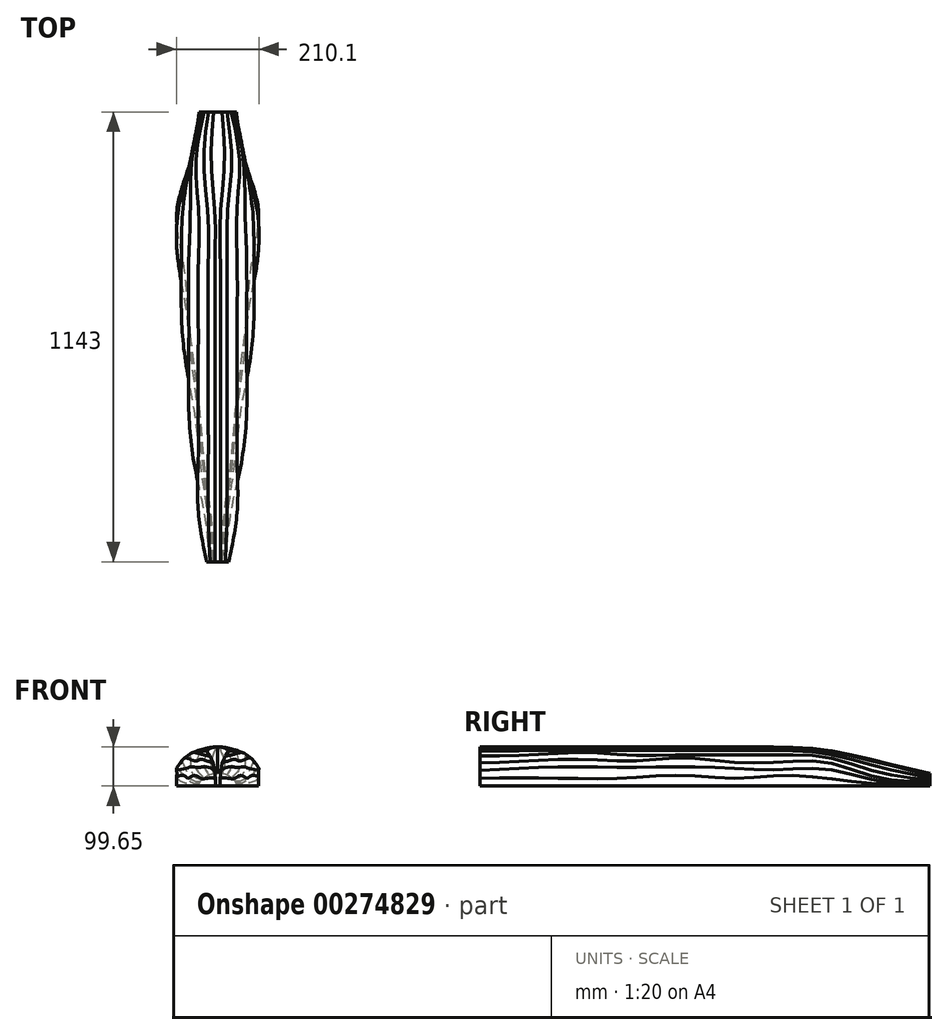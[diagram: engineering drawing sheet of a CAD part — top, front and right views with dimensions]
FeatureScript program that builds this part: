
annotation { "Feature Type Name" : "Feature", "Feature Type Description" : "" }
export const myFeature = defineFeature(function(context is Context, id is Id, definition is map)
    precondition{}
    {
        {
            var Q0;
            Q0=qCreatedBy(makeId("Front.planeOp"),FACE);
            cPlane(context, id + "F0", {"entities" : qUnion([Q0]), "cplaneType" : CPlaneType.OFFSET, "offset" : 127 * mm, "oppositeDirection" : true, "width" : 152.4 * mm, "height" : 152.4 * mm});
        }
        {
            var Q0;
            Q0=qCreatedBy(makeId("Front.planeOp"),FACE);
            cPlane(context, id + "F1", {"entities" : qUnion([Q0]), "cplaneType" : CPlaneType.OFFSET, "offset" : 254 * mm, "oppositeDirection" : true, "width" : 152.4 * mm, "height" : 152.4 * mm});
        }
        {
            var Q0;
            Q0=qCreatedBy(makeId("Front.planeOp"),FACE);
            cPlane(context, id + "F2", {"entities" : qUnion([Q0]), "cplaneType" : CPlaneType.OFFSET, "offset" : 381 * mm, "oppositeDirection" : true, "width" : 152.4 * mm, "height" : 152.4 * mm});
        }
        {
            var Q0;
            Q0=qCreatedBy(makeId("Front.planeOp"),FACE);
            cPlane(context, id + "F3", {"entities" : qUnion([Q0]), "cplaneType" : CPlaneType.OFFSET, "offset" : 127 * mm, "width" : 152.4 * mm, "height" : 152.4 * mm});
        }
        {
            var Q0;
            Q0=qCreatedBy(makeId("Front.planeOp"),FACE);
            cPlane(context, id + "F4", {"entities" : qUnion([Q0]), "cplaneType" : CPlaneType.OFFSET, "offset" : 254 * mm, "width" : 152.4 * mm, "height" : 152.4 * mm});
        }
        {
            var Q0;
            Q0=qCreatedBy(makeId("Front.planeOp"),FACE);
            cPlane(context, id + "F5", {"entities" : qUnion([Q0]), "cplaneType" : CPlaneType.OFFSET, "offset" : 381 * mm, "width" : 152.4 * mm, "height" : 152.4 * mm});
        }
        {
            var Q0;
            Q0=qCreatedBy(makeId("Front.planeOp"),FACE);
            cPlane(context, id + "F6", {"entities" : qUnion([Q0]), "cplaneType" : CPlaneType.OFFSET, "offset" : 508 * mm, "width" : 152.4 * mm, "height" : 152.4 * mm});
        }
        {
            var Q0;
            Q0=qCreatedBy(id+"F2.planeOp",FACE);
            var sketch = newSketch(context, id + "F7", { "sketchPlane" : qUnion([Q0])});
            skLineSegment(sketch, "E0", {"start": v(-55.45, -58.67) * mm, "end": v(48.5, -58.67) * mm});
            skLineSegment(sketch, "E1", {"start": v(48.5, -58.67) * mm, "end": v(48.5, -39.44) * mm});
            skLineSegment(sketch, "E2", {"start": v(48.5, -39.44) * mm, "end": v(45.16, -16.7) * mm});
            skLineSegment(sketch, "E3", {"start": v(45.16, -16.7) * mm, "end": v(33.42, 0) * mm});
            skLineSegment(sketch, "E4", {"start": v(33.42, 0) * mm, "end": v(13.96, 12.38) * mm});
            skLineSegment(sketch, "E5", {"start": v(13.96, 12.38) * mm, "end": v(-7.08, 22.02) * mm});
            skLineSegment(sketch, "E6", {"start": v(-7.08, 22.02) * mm, "end": v(-30.27, 29.1) * mm});
            skLineSegment(sketch, "E7", {"start": v(-30.27, 29.1) * mm, "end": v(-48.16, 31.65) * mm});
            skLineSegment(sketch, "E8", {"start": v(-48.16, 31.65) * mm, "end": v(-55.45, 31.65) * mm});
            skLineSegment(sketch, "E9", {"start": v(-55.45, 31.65) * mm, "end": v(-55.45, -58.67) * mm});
            skSolve(sketch);
        }
        {
            var Q0;
            Q0=qCreatedBy(id+"F1.planeOp",FACE);
            var sketch = newSketch(context, id + "F8", { "sketchPlane" : qUnion([Q0])});
            skLineSegment(sketch, "E10", {"start": v(-55.45, -58.67) * mm, "end": v(31.61, -58.67) * mm});
            skLineSegment(sketch, "E11", {"start": v(31.61, -58.67) * mm, "end": v(31.61, -32) * mm});
            skLineSegment(sketch, "E12", {"start": v(31.61, -32) * mm, "end": v(44.98, -17.07) * mm});
            skLineSegment(sketch, "E13", {"start": v(44.98, -17.07) * mm, "end": v(36.88, 2.51) * mm});
            skLineSegment(sketch, "E14", {"start": v(36.88, 2.51) * mm, "end": v(18.07, 20.36) * mm});
            skLineSegment(sketch, "E15", {"start": v(18.07, 20.36) * mm, "end": v(-6.04, 31.25) * mm});
            skLineSegment(sketch, "E16", {"start": v(-6.04, 31.25) * mm, "end": v(-31.47, 38.05) * mm});
            skLineSegment(sketch, "E17", {"start": v(-31.47, 38.05) * mm, "end": v(-48.7, 40.66) * mm});
            skLineSegment(sketch, "E18", {"start": v(-48.7, 40.66) * mm, "end": v(-55.45, 40.66) * mm});
            skLineSegment(sketch, "E19", {"start": v(-55.45, 40.66) * mm, "end": v(-55.45, -58.67) * mm});
            skSolve(sketch);
        }
        {
            var Q0;
            Q0=qCreatedBy(id+"F0.planeOp",FACE);
            var sketch = newSketch(context, id + "F9", { "sketchPlane" : qUnion([Q0])});
            skLineSegment(sketch, "E20", {"start": v(-55.45, -58.67) * mm, "end": v(19.66, -58.67) * mm});
            skLineSegment(sketch, "E21", {"start": v(19.66, -58.67) * mm, "end": v(19.66, -38.92) * mm});
            skLineSegment(sketch, "E22", {"start": v(19.66, -38.92) * mm, "end": v(22.96, -13.33) * mm});
            skLineSegment(sketch, "E23", {"start": v(22.96, -13.33) * mm, "end": v(36.88, 2.51) * mm});
            skLineSegment(sketch, "E24", {"start": v(36.88, 2.51) * mm, "end": v(18.07, 20.36) * mm});
            skLineSegment(sketch, "E25", {"start": v(18.07, 20.36) * mm, "end": v(-6.04, 31.25) * mm});
            skLineSegment(sketch, "E26", {"start": v(-6.04, 31.25) * mm, "end": v(-31.47, 38.05) * mm});
            skLineSegment(sketch, "E27", {"start": v(-31.47, 38.05) * mm, "end": v(-48.7, 40.66) * mm});
            skLineSegment(sketch, "E28", {"start": v(-48.7, 40.66) * mm, "end": v(-55.45, 40.66) * mm});
            skLineSegment(sketch, "E29", {"start": v(-55.45, 40.66) * mm, "end": v(-55.45, -58.67) * mm});
            skSolve(sketch);
        }
        {
            var Q0;
            Q0=qCreatedBy(makeId("Front.planeOp"),FACE);
            var sketch = newSketch(context, id + "F10", { "sketchPlane" : qUnion([Q0])});
            skLineSegment(sketch, "E30", {"start": v(-55.45, -58.67) * mm, "end": v(4.91, -58.67) * mm});
            skLineSegment(sketch, "E31", {"start": v(4.91, -58.67) * mm, "end": v(4.91, -31.45) * mm});
            skLineSegment(sketch, "E32", {"start": v(4.91, -31.45) * mm, "end": v(10.42, -9.63) * mm});
            skLineSegment(sketch, "E33", {"start": v(10.42, -9.63) * mm, "end": v(26.15, 12.58) * mm});
            skLineSegment(sketch, "E34", {"start": v(26.15, 12.58) * mm, "end": v(18.28, 20.25) * mm});
            skLineSegment(sketch, "E35", {"start": v(18.28, 20.25) * mm, "end": v(-6.04, 31.25) * mm});
            skLineSegment(sketch, "E36", {"start": v(-6.04, 31.25) * mm, "end": v(-31.47, 38.05) * mm});
            skLineSegment(sketch, "E37", {"start": v(-31.47, 38.05) * mm, "end": v(-48.7, 40.66) * mm});
            skLineSegment(sketch, "E38", {"start": v(-48.7, 40.66) * mm, "end": v(-55.45, 40.66) * mm});
            skLineSegment(sketch, "E39", {"start": v(-55.45, 40.66) * mm, "end": v(-55.45, -58.67) * mm});
            skSolve(sketch);
        }
        {
            var Q0;
            Q0=qCreatedBy(id+"F3.planeOp",FACE);
            var sketch = newSketch(context, id + "F11", { "sketchPlane" : qUnion([Q0])});
            skLineSegment(sketch, "E40", {"start": v(-55.45, -58.67) * mm, "end": v(-10.42, -58.67) * mm});
            skLineSegment(sketch, "E41", {"start": v(-10.42, -58.67) * mm, "end": v(-10.42, -38.14) * mm});
            skLineSegment(sketch, "E42", {"start": v(-10.42, -38.14) * mm, "end": v(-6.1, -11.8) * mm});
            skLineSegment(sketch, "E43", {"start": v(-6.1, -11.8) * mm, "end": v(3.34, 4.72) * mm});
            skLineSegment(sketch, "E44", {"start": v(3.34, 4.72) * mm, "end": v(18.09, 20.05) * mm});
            skLineSegment(sketch, "E45", {"start": v(18.09, 20.05) * mm, "end": v(-6.04, 31.25) * mm});
            skLineSegment(sketch, "E46", {"start": v(-6.04, 31.25) * mm, "end": v(-31.47, 38.05) * mm});
            skLineSegment(sketch, "E47", {"start": v(-31.47, 38.05) * mm, "end": v(-48.7, 40.66) * mm});
            skLineSegment(sketch, "E48", {"start": v(-48.7, 40.66) * mm, "end": v(-55.45, 40.66) * mm});
            skLineSegment(sketch, "E49", {"start": v(-55.45, 40.66) * mm, "end": v(-55.45, -58.67) * mm});
            skSolve(sketch);
        }
        {
            var Q0;
            Q0=qCreatedBy(id+"F4.planeOp",FACE);
            var sketch = newSketch(context, id + "F12", { "sketchPlane" : qUnion([Q0])});
            skLineSegment(sketch, "E50", {"start": v(-55.45, -58.67) * mm, "end": v(-21.43, -58.67) * mm});
            skLineSegment(sketch, "E51", {"start": v(-21.43, -58.67) * mm, "end": v(-21.43, -39.9) * mm});
            skLineSegment(sketch, "E52", {"start": v(-21.43, -39.9) * mm, "end": v(-17.5, -9.83) * mm});
            skLineSegment(sketch, "E53", {"start": v(-17.5, -9.83) * mm, "end": v(-11.2, 9.24) * mm});
            skLineSegment(sketch, "E54", {"start": v(-11.2, 9.24) * mm, "end": v(5.11, 26.34) * mm});
            skLineSegment(sketch, "E55", {"start": v(5.11, 26.34) * mm, "end": v(-6.04, 31.25) * mm});
            skLineSegment(sketch, "E56", {"start": v(-6.04, 31.25) * mm, "end": v(-31.47, 38.05) * mm});
            skLineSegment(sketch, "E57", {"start": v(-31.47, 38.05) * mm, "end": v(-48.7, 40.66) * mm});
            skLineSegment(sketch, "E58", {"start": v(-48.7, 40.66) * mm, "end": v(-55.45, 40.66) * mm});
            skLineSegment(sketch, "E59", {"start": v(-55.45, 40.66) * mm, "end": v(-55.45, -58.67) * mm});
            skSolve(sketch);
        }
        {
            var Q0;
            Q0=qCreatedBy(id+"F5.planeOp",FACE);
            var sketch = newSketch(context, id + "F13", { "sketchPlane" : qUnion([Q0])});
            skLineSegment(sketch, "E60", {"start": v(-55.45, -58.67) * mm, "end": v(-37.94, -58.67) * mm});
            skLineSegment(sketch, "E61", {"start": v(-37.94, -58.67) * mm, "end": v(-37.94, -37.94) * mm});
            skLineSegment(sketch, "E62", {"start": v(-37.94, -37.94) * mm, "end": v(-34.4, -12) * mm});
            skLineSegment(sketch, "E63", {"start": v(-34.4, -12) * mm, "end": v(-29.68, 4.91) * mm});
            skLineSegment(sketch, "E64", {"start": v(-21.23, 20.05) * mm, "end": v(-29.68, 4.91) * mm});
            skLineSegment(sketch, "E65", {"start": v(-21.23, 20.05) * mm, "end": v(-6.04, 31.25) * mm});
            skLineSegment(sketch, "E66", {"start": v(-6.04, 31.25) * mm, "end": v(-31.47, 38.05) * mm});
            skLineSegment(sketch, "E67", {"start": v(-31.47, 38.05) * mm, "end": v(-48.7, 40.66) * mm});
            skLineSegment(sketch, "E68", {"start": v(-48.7, 40.66) * mm, "end": v(-55.45, 40.66) * mm});
            skLineSegment(sketch, "E69", {"start": v(-55.45, 40.66) * mm, "end": v(-55.45, -58.67) * mm});
            skSolve(sketch);
        }
        {
            var Q0;
            Q0=qCreatedBy(id+"F6.planeOp",FACE);
            var sketch = newSketch(context, id + "F14", { "sketchPlane" : qUnion([Q0])});
            skLineSegment(sketch, "E70", {"start": v(-55.45, -58.67) * mm, "end": v(-49.54, -58.67) * mm});
            skLineSegment(sketch, "E71", {"start": v(-49.54, -58.67) * mm, "end": v(-49.54, -39.71) * mm});
            skLineSegment(sketch, "E72", {"start": v(-49.54, -39.71) * mm, "end": v(-47.18, -19.27) * mm});
            skLineSegment(sketch, "E73", {"start": v(-47.18, -19.27) * mm, "end": v(-43.84, 0) * mm});
            skLineSegment(sketch, "E74", {"start": v(-43.84, 0) * mm, "end": v(-35.98, 18.48) * mm});
            skLineSegment(sketch, "E75", {"start": v(-35.98, 18.48) * mm, "end": v(-27.52, 30.47) * mm});
            skLineSegment(sketch, "E76", {"start": v(-27.52, 30.47) * mm, "end": v(-35.78, 36.56) * mm});
            skLineSegment(sketch, "E77", {"start": v(-35.78, 36.56) * mm, "end": v(-48.7, 40.66) * mm});
            skLineSegment(sketch, "E78", {"start": v(-48.7, 40.66) * mm, "end": v(-55.45, 40.66) * mm});
            skLineSegment(sketch, "E79", {"start": v(-55.45, 40.66) * mm, "end": v(-55.45, -58.67) * mm});
            skSolve(sketch);
        }
        {
            var Q0;
            Q0=qCreatedBy(makeId("Front.planeOp"),FACE);
            cPlane(context, id + "F15", {"entities" : qUnion([Q0]), "cplaneType" : CPlaneType.OFFSET, "offset" : 508 * mm, "oppositeDirection" : true, "width" : 152.4 * mm, "height" : 152.4 * mm});
        }
        {
            var Q0;
            Q0=qCreatedBy(makeId("Front.planeOp"),FACE);
            cPlane(context, id + "F16", {"entities" : qUnion([Q0]), "cplaneType" : CPlaneType.OFFSET, "offset" : 635 * mm, "oppositeDirection" : true, "width" : 152.4 * mm, "height" : 152.4 * mm});
        }
        {
            var Q0;
            Q0=qCreatedBy(id+"F15.planeOp",FACE);
            var sketch = newSketch(context, id + "F17", { "sketchPlane" : qUnion([Q0])});
            skLineSegment(sketch, "E80", {"start": v(-55.45, -58.67) * mm, "end": v(14.39, -58.67) * mm});
            skLineSegment(sketch, "E81", {"start": v(14.39, -58.67) * mm, "end": v(14.39, -53.58) * mm});
            skLineSegment(sketch, "E82", {"start": v(14.39, -53.58) * mm, "end": v(14.63, -46.57) * mm});
            skLineSegment(sketch, "E83", {"start": v(14.63, -46.57) * mm, "end": v(14.59, -38.3) * mm});
            skLineSegment(sketch, "E84", {"start": v(14.59, -38.3) * mm, "end": v(10.13, -24.95) * mm});
            skLineSegment(sketch, "E85", {"start": v(10.13, -24.95) * mm, "end": v(0, -11.24) * mm});
            skLineSegment(sketch, "E86", {"start": v(0, -11.24) * mm, "end": v(-19.82, 0) * mm});
            skLineSegment(sketch, "E87", {"start": v(-19.82, 0) * mm, "end": v(-38.22, 2.96) * mm});
            skLineSegment(sketch, "E88", {"start": v(-38.22, 2.96) * mm, "end": v(-55.45, 2.96) * mm});
            skLineSegment(sketch, "E89", {"start": v(-55.45, 2.96) * mm, "end": v(-55.45, -58.67) * mm});
            skSolve(sketch);
        }
        {
            var Q0;
            Q0=qCreatedBy(id+"F16.planeOp",FACE);
            var sketch = newSketch(context, id + "F18", { "sketchPlane" : qUnion([Q0])});
            skLineSegment(sketch, "E90", {"start": v(-55.45, -58.67) * mm, "end": v(-8.16, -58.67) * mm});
            skLineSegment(sketch, "E91", {"start": v(-8.16, -58.67) * mm, "end": v(-8.16, -53.47) * mm});
            skLineSegment(sketch, "E92", {"start": v(-8.16, -53.47) * mm, "end": v(-8.94, -50.33) * mm});
            skLineSegment(sketch, "E93", {"start": v(-8.94, -50.33) * mm, "end": v(-10.52, -46.4) * mm});
            skLineSegment(sketch, "E94", {"start": v(-10.52, -46.4) * mm, "end": v(-14.25, -42.66) * mm});
            skLineSegment(sketch, "E95", {"start": v(-14.25, -42.66) * mm, "end": v(-20.94, -37.55) * mm});
            skLineSegment(sketch, "E96", {"start": v(-20.94, -37.55) * mm, "end": v(-32.14, -30.08) * mm});
            skLineSegment(sketch, "E97", {"start": v(-32.14, -30.08) * mm, "end": v(-44.72, -26.34) * mm});
            skLineSegment(sketch, "E98", {"start": v(-44.72, -26.34) * mm, "end": v(-55.45, -26.34) * mm});
            skLineSegment(sketch, "E99", {"start": v(-55.45, -26.34) * mm, "end": v(-55.45, -58.67) * mm});
            skSolve(sketch);
        }
        {
            var Q0;
            Q0=makeQuery(id+"F14.imprint","IMPRINT",FACE,{"disambiguationData":[TD([[makeQuery(id+"F14.imprint","IMPRINT",EDGE,{"derivedFrom":sQuery(id+"F14.wireOp",EDGE,"E70")}),1.0]])]});
            var Q1;
            Q1=makeQuery(id+"F13.imprint","IMPRINT",FACE,{"disambiguationData":[TD([[makeQuery(id+"F13.imprint","IMPRINT",EDGE,{"derivedFrom":sQuery(id+"F13.wireOp",EDGE,"E60")}),1.0]])]});
            var Q2;
            Q2=makeQuery(id+"F12.imprint","IMPRINT",FACE,{"disambiguationData":[TD([[makeQuery(id+"F12.imprint","IMPRINT",EDGE,{"derivedFrom":sQuery(id+"F12.wireOp",EDGE,"E50")}),1.0]])]});
            var Q3;
            Q3=makeQuery(id+"F11.imprint","IMPRINT",FACE,{"disambiguationData":[TD([[makeQuery(id+"F11.imprint","IMPRINT",EDGE,{"derivedFrom":sQuery(id+"F11.wireOp",EDGE,"E40")}),1.0]])]});
            var Q4;
            Q4=makeQuery(id+"F10.imprint","IMPRINT",FACE,{"disambiguationData":[TD([[makeQuery(id+"F10.imprint","IMPRINT",EDGE,{"derivedFrom":sQuery(id+"F10.wireOp",EDGE,"E30")}),1.0]])]});
            var Q5;
            Q5=makeQuery(id+"F9.imprint","IMPRINT",FACE,{"disambiguationData":[TD([[makeQuery(id+"F9.imprint","IMPRINT",EDGE,{"derivedFrom":sQuery(id+"F9.wireOp",EDGE,"E20")}),1.0]])]});
            var Q6;
            Q6=makeQuery(id+"F8.imprint","IMPRINT",FACE,{"disambiguationData":[TD([[makeQuery(id+"F8.imprint","IMPRINT",EDGE,{"derivedFrom":sQuery(id+"F8.wireOp",EDGE,"E10")}),1.0]])]});
            var Q7;
            Q7=makeQuery(id+"F7.imprint","IMPRINT",FACE,{"disambiguationData":[TD([[makeQuery(id+"F7.imprint","IMPRINT",EDGE,{"derivedFrom":sQuery(id+"F7.wireOp",EDGE,"E0")}),1.0]])]});
            var Q8;
            Q8=makeQuery(id+"F17.imprint","IMPRINT",FACE,{"disambiguationData":[TD([[makeQuery(id+"F17.imprint","IMPRINT",EDGE,{"derivedFrom":sQuery(id+"F17.wireOp",EDGE,"E80")}),1.0]])]});
            var Q9;
            Q9=makeQuery(id+"F18.imprint","IMPRINT",FACE,{"disambiguationData":[TD([[makeQuery(id+"F18.imprint","IMPRINT",EDGE,{"derivedFrom":sQuery(id+"F18.wireOp",EDGE,"E90")}),1.0]])]});
            loft(context, id + "F19", {"sheetProfilesArray" : [{ "sheetProfileEntities" : qUnion([Q0]) }, { "sheetProfileEntities" : qUnion([Q1]) }, { "sheetProfileEntities" : qUnion([Q2]) }, { "sheetProfileEntities" : qUnion([Q3]) }, { "sheetProfileEntities" : qUnion([Q4]) }, { "sheetProfileEntities" : qUnion([Q5]) }, { "sheetProfileEntities" : qUnion([Q6]) }, { "sheetProfileEntities" : qUnion([Q7]) }, { "sheetProfileEntities" : qUnion([Q8]) }, { "sheetProfileEntities" : qUnion([Q9]) }]});
        }
        {
            var Q0;
            Q0=makeQuery(id+"F19.opLoft","SWEPT_BODY",BODY,{"disambiguationData":[OSD([sQuery(id+"F7.wireOp",EDGE,"E6"),sQuery(id+"F8.wireOp",EDGE,"E16"),sQuery(id+"F9.wireOp",EDGE,"E26"),sQuery(id+"F10.wireOp",EDGE,"E36"),sQuery(id+"F11.wireOp",EDGE,"E46"),sQuery(id+"F12.wireOp",EDGE,"E56"),sQuery(id+"F13.wireOp",EDGE,"E66"),makeQuery(id+"F14.imprint","IMPRINT",FACE,{"disambiguationData":[TD([[makeQuery(id+"F14.imprint","IMPRINT",EDGE,{"derivedFrom":sQuery(id+"F14.wireOp",EDGE,"E70")}),1.0]])]}),sQuery(id+"F17.wireOp",EDGE,"E86"),makeQuery(id+"F18.imprint","IMPRINT",FACE,{"disambiguationData":[TD([[makeQuery(id+"F18.imprint","IMPRINT",EDGE,{"derivedFrom":sQuery(id+"F18.wireOp",EDGE,"E90")}),1.0]])]})])]});
            var Q1;
            Q1=makeQuery(id+"F19.opLoft","SWEPT_FACE",FACE,{"disambiguationData":[OSD([sQuery(id+"F13.wireOp",EDGE,"E60"),sQuery(id+"F13.wireOp",EDGE,"E68"),sQuery(id+"F13.wireOp",EDGE,"E69"),sQuery(id+"F14.wireOp",EDGE,"E70"),sQuery(id+"F14.wireOp",EDGE,"E78"),sQuery(id+"F14.wireOp",EDGE,"E79")])]});
            mirror(context, id + "F20", {"operationType" : NewBodyOperationType.ADD, "entities" : qUnion([Q0]), "mirrorPlane" : qUnion([Q1])});
        }
    });
